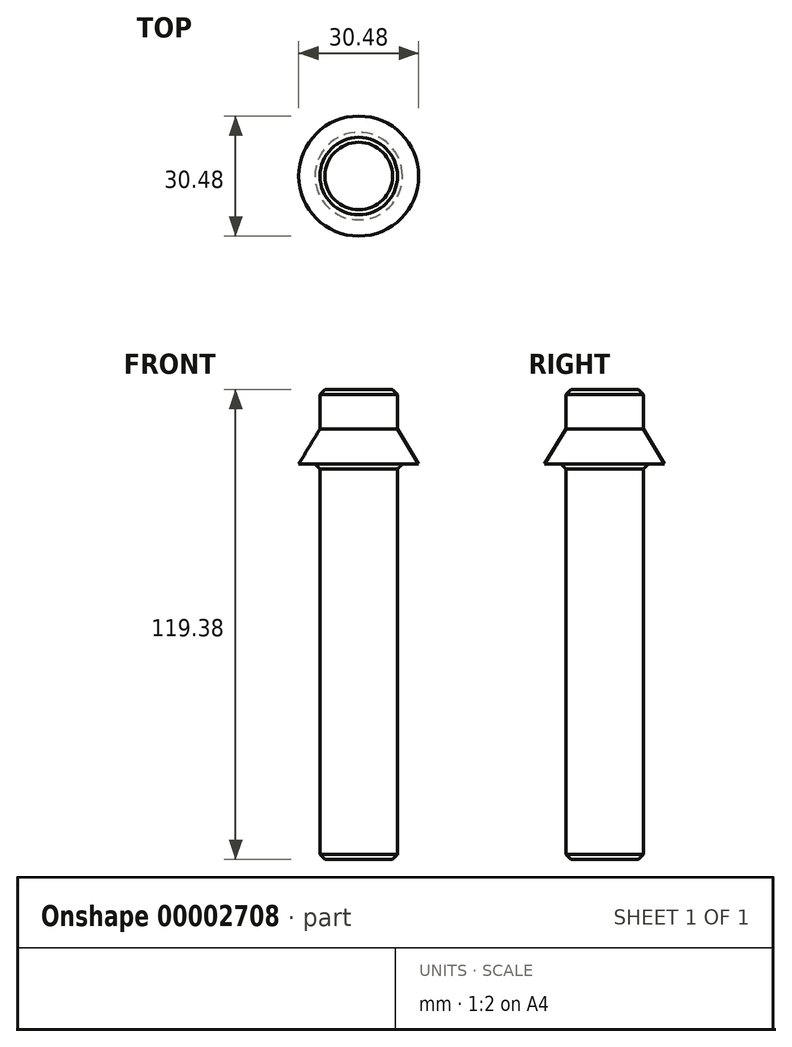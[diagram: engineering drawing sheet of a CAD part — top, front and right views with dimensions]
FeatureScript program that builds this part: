
annotation { "Feature Type Name" : "Feature", "Feature Type Description" : "" }
export const myFeature = defineFeature(function(context is Context, id is Id, definition is map)
    precondition{}
    {
        {
            var Q0;
            Q0=qCreatedBy(makeId("Top.planeOp"),FACE);
            var sketch = newSketch(context, id + "F0", { "sketchPlane" : qUnion([Q0])});
            skCircle(sketch, "E0", {"center": v(0, 0) * mm, "radius": 9.84 * mm});
            skSolve(sketch);
        }
        {
            var Q0;
            Q0 = qSketchRegion(id + "F0", true);
            extrude(context, id + "F1", {"entities" : qUnion([Q0]), "depth" : 119.38 * mm});
        }
        {
            var Q0;
            Q0=qCreatedBy(makeId("Front.planeOp"),FACE);
            var sketch = newSketch(context, id + "F2", { "sketchPlane" : qUnion([Q0])});
            skLineSegment(sketch, "E1.0", {"start": v(-9.84, 119.38) * mm, "end": v(9.84, 119.38) * mm});
            skLineSegment(sketch, "E2", {"start": v(0, 109.38) * mm, "end": v(9.84, 109.38) * mm});
            skLineSegment(sketch, "E3", {"start": v(9.84, 109.38) * mm, "end": v(15.24, 100.49) * mm});
            skLineSegment(sketch, "E4", {"start": v(15.24, 100.49) * mm, "end": v(0, 100.49) * mm});
            skLineSegment(sketch, "E5", {"start": v(0, 100.49) * mm, "end": v(0, 109.38) * mm});
            skSolve(sketch);
        }
        {
            var Q0;
            Q0=makeQuery(id+"F2.imprint","IMPRINT",FACE,{"disambiguationData":[TD([[makeQuery(id+"F2.imprint","IMPRINT",EDGE,{"derivedFrom":sQuery(id+"F2.wireOp",EDGE,"E2")}),-1.0]])]});
            var Q1;
            Q1=sQuery(id+"F2.wireOp",EDGE,"E5");
            revolve(context, id + "F3", {"operationType" : NewBodyOperationType.ADD, "entities" : qUnion([Q0]), "axis" : qUnion([Q1]), "revolveType" : RevolveType.FULL});
        }
        {
            var Q0;
            Q0=makeQuery(id+"F1.opExtrude","CAP_EDGE",EDGE,{"disambiguationData":[OSD([sQuery(id+"F0.wireOp",EDGE,"E0")])],"isStart":true});
            var Q1;
            Q1=makeQuery(id+"F3.boolean.opBoolean","INTERSECT",EDGE,{"derivedFrom":[makeQuery(id+"F1.opExtrude","SWEPT_FACE",FACE,{"disambiguationData":[OSD([sQuery(id+"F0.wireOp",EDGE,"E0")])]}),makeQuery(id+"F3.opRevolve","SWEPT_FACE",FACE,{"disambiguationData":[OSD([sQuery(id+"F2.wireOp",EDGE,"E4")])]})]});
            var Q2;
            Q2=makeQuery(id+"F1.opExtrude","CAP_EDGE",EDGE,{"disambiguationData":[OSD([sQuery(id+"F0.wireOp",EDGE,"E0")])],"isStart":false});
            chamfer(context, id + "F4", {"entities" : qUnion([Q0, Q1, Q2]), "width" : 1.27 * mm, "tangentPropagation" : true});
        }
    });
